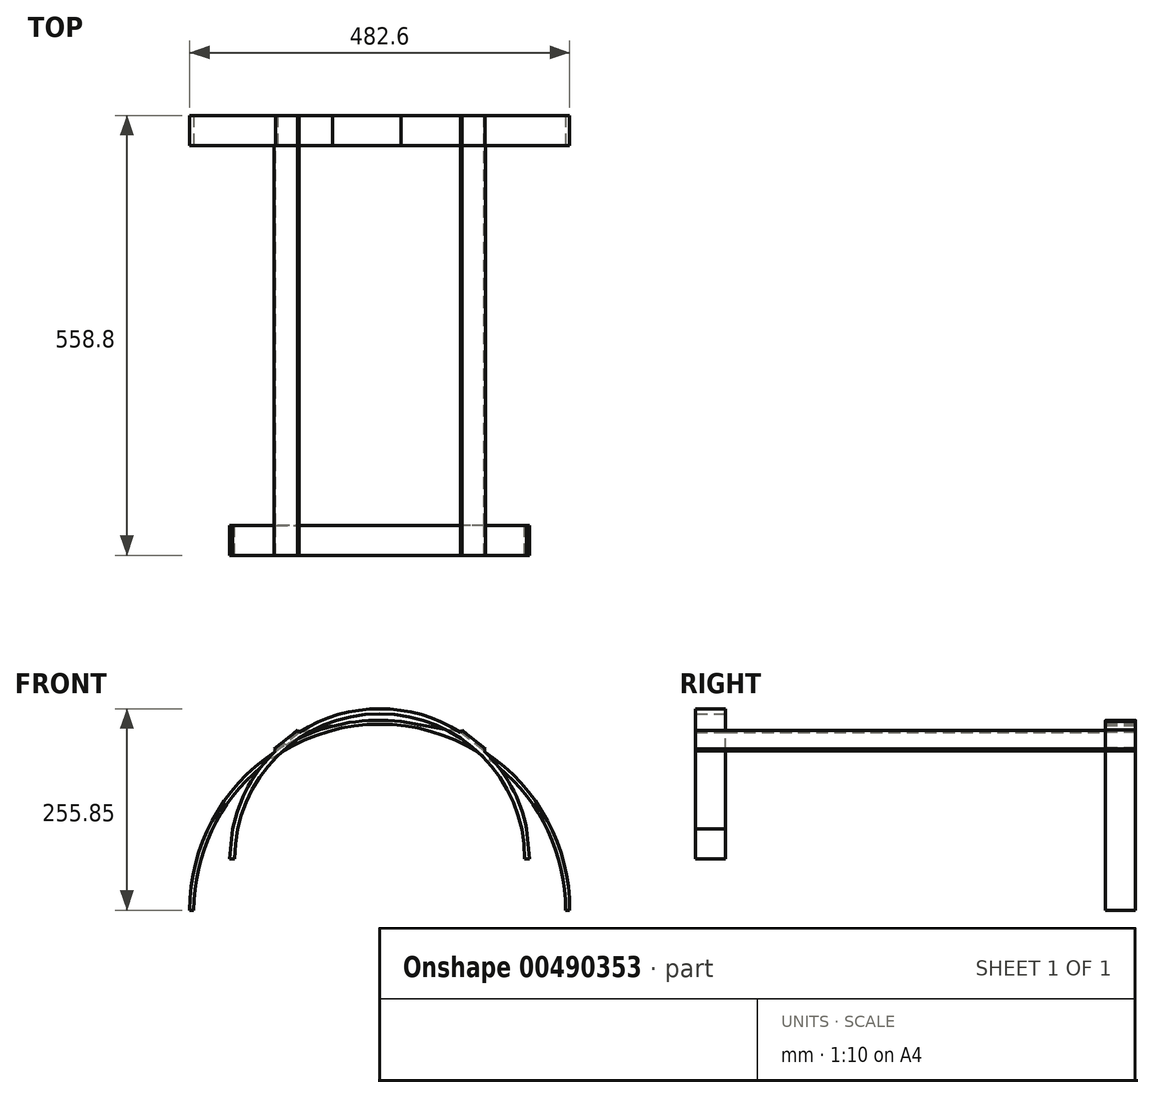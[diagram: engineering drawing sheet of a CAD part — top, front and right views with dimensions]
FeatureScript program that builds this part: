
annotation { "Feature Type Name" : "Feature", "Feature Type Description" : "" }
export const myFeature = defineFeature(function(context is Context, id is Id, definition is map)
    precondition{}
    {
        {
            var Q0;
            Q0=qCreatedBy(makeId("Front.planeOp"),FACE);
            var sketch = newSketch(context, id + "F0", { "sketchPlane" : qUnion([Q0])});
            skArc(sketch, "E0", {"start": v(186.7, 37.9) * mm, "mid": v(167, 91.68) * mm, "end": v(132.2, 137.16) * mm});
            skLineSegment(sketch, "E1", {"start": v(-190.5, 0) * mm, "end": v(-184.15, 0) * mm});
            skLineSegment(sketch, "E2", {"start": v(-132.2, 137.16) * mm, "end": v(-102.26, 160.72) * mm});
            skLineSegment(sketch, "E3", {"start": v(132.2, 137.16) * mm, "end": v(102.26, 160.72) * mm});
            skArc(sketch, "E4.trimOffspring", {"start": v(-132.2, 137.16) * mm, "mid": v(-167, 91.68) * mm, "end": v(-186.7, 37.9) * mm});
            skArc(sketch, "E5.trimOffspring", {"start": v(102.26, 160.72) * mm, "mid": v(0, 190.5) * mm, "end": v(-102.26, 160.72) * mm});
            skLineSegment(sketch, "E6", {"start": v(-190.5, 0) * mm, "end": v(-186.7, 37.9) * mm});
            skLineSegment(sketch, "E7", {"start": v(190.5, 0) * mm, "end": v(186.7, 37.9) * mm});
            skArc(sketch, "E8", {"start": v(184.15, 0) * mm, "mid": v(0, 184.15) * mm, "end": v(-184.15, 0) * mm});
            skLineSegment(sketch, "E9.trimOffspring", {"start": v(184.15, 0) * mm, "end": v(190.5, 0) * mm});
            skSolve(sketch);
        }
        {
            var Q0;
            Q0 = qSketchRegion(id + "F0", true);
            extrude(context, id + "F1", {"entities" : qUnion([Q0]), "depth" : 38.1 * mm});
        }
        {
            var Q0;
            Q0=makeQuery(id+"F1.opExtrude","SWEPT_FACE",FACE,{"disambiguationData":[OSD([sQuery(id+"F0.wireOp",EDGE,"E2")])]});
            var sketch = newSketch(context, id + "F2", { "sketchPlane" : qUnion([Q0])});
            skLineSegment(sketch, "E10", {"start": v(-19.05, 0) * mm, "end": v(-19.05, 482.6) * mm});
            skLineSegment(sketch, "E11", {"start": v(19.05, 0) * mm, "end": v(19.05, 482.6) * mm});
            skLineSegment(sketch, "E12", {"start": v(19.05, 482.6) * mm, "end": v(-19.05, 482.6) * mm});
            skLineSegment(sketch, "E13", {"start": v(-19.05, 0) * mm, "end": v(-19.05, -38.1) * mm});
            skLineSegment(sketch, "E14", {"start": v(-19.05, -38.1) * mm, "end": v(19.05, -38.1) * mm});
            skLineSegment(sketch, "E15", {"start": v(19.05, -38.1) * mm, "end": v(19.05, 0) * mm});
            skSolve(sketch);
        }
        {
            var Q0;
            Q0=makeQuery(id+"F2.imprint","IMPRINT",FACE,{"disambiguationData":[TD([[makeQuery(id+"F2.imprint","IMPRINT",EDGE,{"derivedFrom":sQuery(id+"F2.wireOp",EDGE,"E13")}),-1.0]])]});
            var Q1;
            Q1=makeQuery(id+"F2.imprint","IMPRINT",FACE,{"disambiguationData":[TD([[makeQuery(id+"F2.imprint","IMPRINT",EDGE,{"derivedFrom":sQuery(id+"F2.wireOp",EDGE,"E10")}),-1.0]])]});
            extrude(context, id + "F3", {"entities" : qUnion([Q0, Q1]), "operationType" : NewBodyOperationType.ADD, "depth" : 3.17 * mm});
        }
        {
            var Q0;
            Q0=makeQuery(id+"F1.opExtrude","SWEPT_FACE",FACE,{"disambiguationData":[OSD([sQuery(id+"F0.wireOp",EDGE,"E3")])]});
            var sketch = newSketch(context, id + "F4", { "sketchPlane" : qUnion([Q0])});
            skLineSegment(sketch, "E16", {"start": v(-19.05, 0) * mm, "end": v(-19.05, 482.6) * mm});
            skLineSegment(sketch, "E17", {"start": v(19.05, 0) * mm, "end": v(19.05, 482.6) * mm});
            skLineSegment(sketch, "E18", {"start": v(19.05, 482.6) * mm, "end": v(-19.05, 482.6) * mm});
            skSolve(sketch);
        }
        {
            var Q0;
            {var subQ0=sQuery(id+"F0.wireOp",EDGE,"E3");Q0=makeQuery(id+"F4.imprint","IMPRINT",FACE,{"disambiguationData":[TD([[makeQuery(id+"F4.imprint","IMPRINT",EDGE,{"derivedFrom":makeQuery(id+"F1.opExtrude","CAP_EDGE",EDGE,{"disambiguationData":[OSD([subQ0])],"isStart":true})}),1.0]])]});}
            var Q1;
            Q1=makeQuery(id+"F4.imprint","IMPRINT",FACE,{"disambiguationData":[TD([[makeQuery(id+"F4.imprint","IMPRINT",EDGE,{"derivedFrom":sQuery(id+"F4.wireOp",EDGE,"E16")}),-1.0]])]});
            extrude(context, id + "F5", {"entities" : qUnion([Q0, Q1]), "operationType" : NewBodyOperationType.ADD, "depth" : 3.17 * mm});
        }
        {
            var Q0;
            Q0=makeQuery(id+"F5.opExtrude","SWEPT_FACE",FACE,{"disambiguationData":[OSD([sQuery(id+"F4.wireOp",EDGE,"E18")])]});
            var sketch = newSketch(context, id + "F6", { "sketchPlane" : qUnion([Q0])});
            skArc(sketch, "E19", {"start": v(241.3, -65.35) * mm, "mid": v(0, 175.95) * mm, "end": v(-241.3, -65.35) * mm});
            skLineSegment(sketch, "E20", {"start": v(-236.22, -65.35) * mm, "end": v(-241.3, -65.35) * mm});
            skLineSegment(sketch, "E21", {"start": v(236.22, -65.35) * mm, "end": v(241.3, -65.35) * mm});
            skLineSegment(sketch, "E22", {"start": v(-102.26, 160.72) * mm, "end": v(-27.3, 174.4) * mm});
            skLineSegment(sketch, "E23", {"start": v(-102.26, 160.72) * mm, "end": v(-131.76, 136.8) * mm});
            skArc(sketch, "E24", {"start": v(236.22, -65.35) * mm, "mid": v(0, 170.87) * mm, "end": v(-236.22, -65.35) * mm});
            skSolve(sketch);
        }
        {
            var Q0;
            Q0=makeQuery(id+"F3.opExtrude","SWEPT_FACE",FACE,{"disambiguationData":[OSD([sQuery(id+"F2.wireOp",EDGE,"E12")])]});
            var sketch = newSketch(context, id + "F7", { "sketchPlane" : qUnion([Q0])});
            skLineSegment(sketch, "E25", {"start": v(102.26, 160.72) * mm, "end": v(27.32, 174.52) * mm});
            skLineSegment(sketch, "E26", {"start": v(102.26, 160.72) * mm, "end": v(132.2, 136.25) * mm});
            skArc(sketch, "E27", {"start": v(241.3, -63.87) * mm, "mid": v(0, 176.06) * mm, "end": v(-241.3, -63.87) * mm});
            skLineSegment(sketch, "E28", {"start": v(-241.3, -63.87) * mm, "end": v(-236.22, -63.87) * mm});
            skArc(sketch, "E29", {"start": v(236.22, -63.87) * mm, "mid": v(0, 170.98) * mm, "end": v(-236.22, -63.87) * mm});
            skLineSegment(sketch, "E30.trimOffspring", {"start": v(236.22, -63.87) * mm, "end": v(241.3, -63.87) * mm});
            skSolve(sketch);
        }
        {
            var Q0;
            {var subQ0=sQuery(id+"F7.wireOp",EDGE,"E26");var subQ4=sQuery(id+"F7.wireOp",EDGE,"E27");var subQ6=makeQuery(id+"F7.imprint","INTERSECT",VERTEX,{"derivedFrom":[subQ0,subQ4]});Q0=makeQuery(id+"F7.imprint","IMPRINT",FACE,{"disambiguationData":[TD([[makeQuery(id+"F7.imprint","IMPRINT",EDGE,{"disambiguationData":[TD([[subQ6,-1.0]])],"derivedFrom":subQ4}),-1.0]])]});}
            extrude(context, id + "F8", {"entities" : qUnion([Q0]), "operationType" : NewBodyOperationType.ADD, "depth" : 38.1 * mm});
        }
        {
            var Q0;
            {var subQ0=sQuery(id+"F6.wireOp",EDGE,"E20");Q0=makeQuery(id+"F6.imprint","IMPRINT",FACE,{"disambiguationData":[TD([[makeQuery(id+"F6.imprint","IMPRINT",EDGE,{"derivedFrom":subQ0}),-1.0]])]});}
            var Q1;
            {var subQ0=sQuery(id+"F6.wireOp",EDGE,"E23");Q1=makeQuery(id+"F6.imprint","IMPRINT",FACE,{"disambiguationData":[TD([[makeQuery(id+"F6.imprint","IMPRINT",EDGE,{"derivedFrom":subQ0}),1.0]])]});}
            extrude(context, id + "F9", {"entities" : qUnion([Q0, Q1]), "depth" : 38.1 * mm});
        }
        {
            var Q0;
            Q0=makeQuery(id+"F9.opExtrude","SWEPT_FACE",FACE,{"disambiguationData":[OSD([sQuery(id+"F6.wireOp",EDGE,"E23")])]});
            var sketch = newSketch(context, id + "F10", { "sketchPlane" : qUnion([Q0])});
            skSolve(sketch);
        }
        {
            var Q0;
            {var subQ0=sQuery(id+"F6.wireOp",EDGE,"E23");Q0=makeQuery(id+"F10.imprint","IMPRINT",FACE,{"disambiguationData":[TD([[makeQuery(id+"F10.imprint","IMPRINT",EDGE,{"derivedFrom":makeQuery(id+"F9.opExtrude","CAP_EDGE",EDGE,{"disambiguationData":[OSD([subQ0])],"isStart":true})}),1.0]])]});}
            extrude(context, id + "F11", {"entities" : qUnion([Q0]), "operationType" : NewBodyOperationType.ADD, "depth" : 3.3 * mm});
        }
        {
            var Q0;
            Q0=makeQuery(id+"F8.opExtrude","SWEPT_FACE",FACE,{"disambiguationData":[OSD([sQuery(id+"F7.wireOp",EDGE,"E26")])]});
            extrude(context, id + "F12", {"entities" : qUnion([Q0]), "operationType" : NewBodyOperationType.ADD, "depth" : 3.3 * mm});
        }
    });
